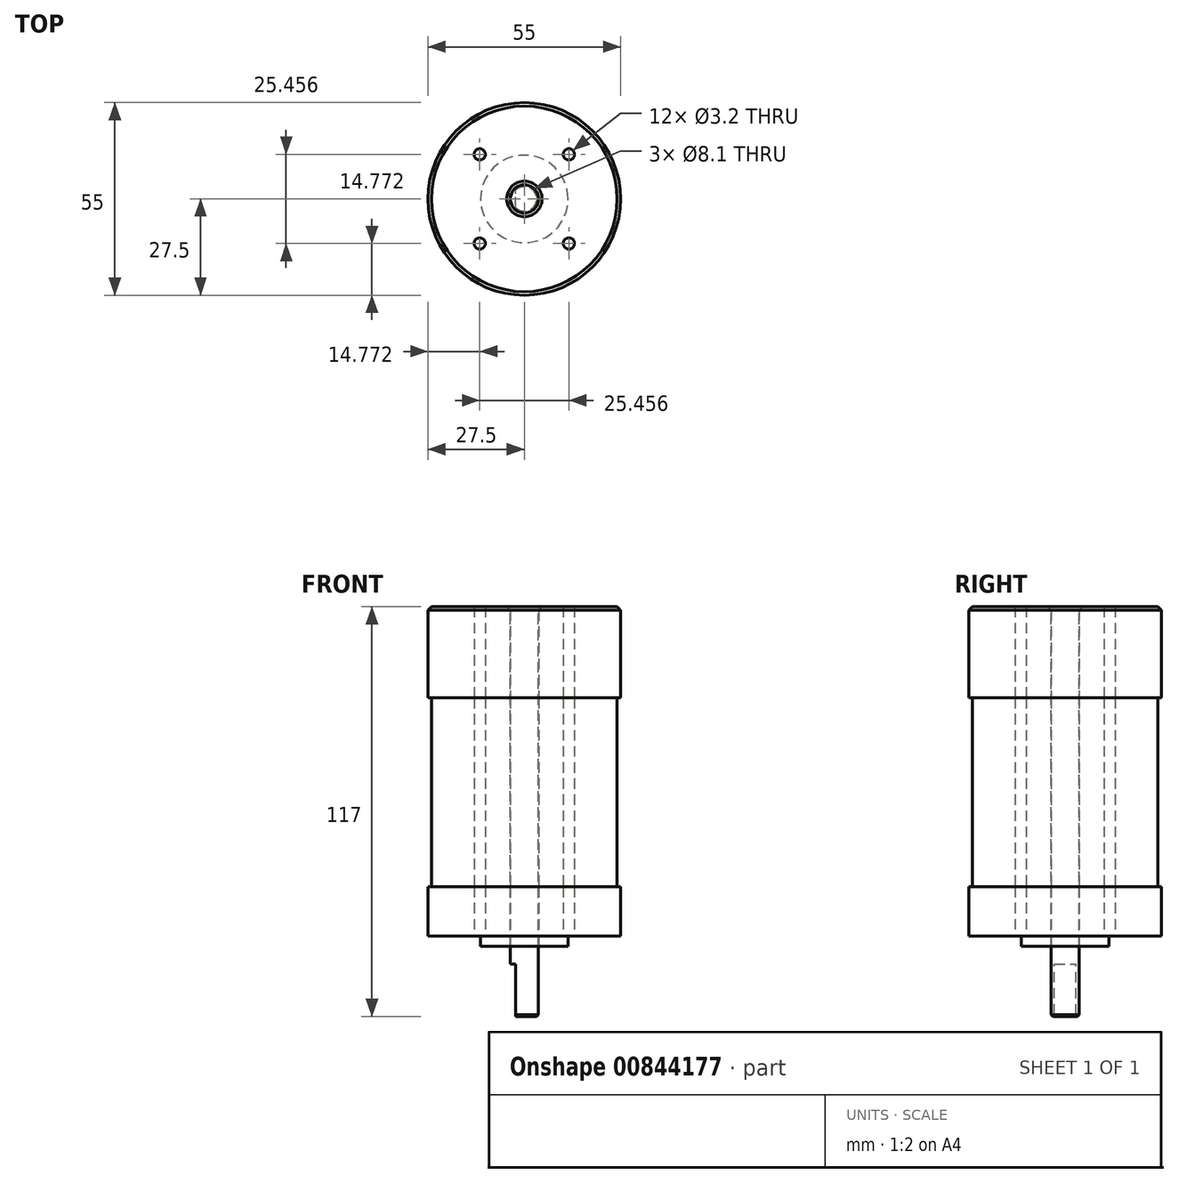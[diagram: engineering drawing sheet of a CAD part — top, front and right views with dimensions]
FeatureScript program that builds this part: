
annotation { "Feature Type Name" : "Feature", "Feature Type Description" : "" }
export const myFeature = defineFeature(function(context is Context, id is Id, definition is map)
    precondition{}
    {
        {
            var Q0;
            Q0=qCreatedBy(makeId("Top.planeOp"),FACE);
            var sketch = newSketch(context, id + "F0", { "sketchPlane" : qUnion([Q0])});
            skCircle(sketch, "E0", {"center": v(0, 0) * mm, "radius": 27.5 * mm});
            skSolve(sketch);
        }
        {
            var Q0;
            Q0=makeQuery(id+"F0.imprint","IMPRINT",FACE,{"disambiguationData":[TD([[makeQuery(id+"F0.imprint","IMPRINT",EDGE,{"derivedFrom":sQuery(id+"F0.wireOp",EDGE,"E0")}),1.0]])]});
            extrude(context, id + "F1", {"entities" : qUnion([Q0]), "depth" : 17 * mm, "offsetDistance" : 25 * mm});
        }
        {
            var Q0;
            Q0=makeQuery(id+"F1.opExtrude","CAP_FACE",FACE,{"disambiguationData":[OSD([sQuery(id+"F0.wireOp",EDGE,"E0")])],"isStart":true});
            var sketch = newSketch(context, id + "F2", { "sketchPlane" : qUnion([Q0])});
            skCircle(sketch, "E1", {"center": v(0, 0) * mm, "radius": 12.5 * mm});
            skSolve(sketch);
        }
        {
            var Q0;
            Q0=makeQuery(id+"F2.imprint","IMPRINT",FACE,{"disambiguationData":[TD([[makeQuery(id+"F2.imprint","IMPRINT",EDGE,{"derivedFrom":sQuery(id+"F2.wireOp",EDGE,"E1")}),-1.0]])]});
            extrude(context, id + "F3", {"entities" : qUnion([Q0]), "operationType" : NewBodyOperationType.REMOVE, "oppositeDirection" : true, "depth" : 3 * mm, "offsetDistance" : 25 * mm});
        }
        {
            var Q0;
            Q0=makeQuery(id+"F1.opExtrude","CAP_FACE",FACE,{"disambiguationData":[OSD([sQuery(id+"F0.wireOp",EDGE,"E0")])],"isStart":false});
            var sketch = newSketch(context, id + "F4", { "sketchPlane" : qUnion([Q0])});
            skCircle(sketch, "E2", {"center": v(0, 0) * mm, "radius": 26.5 * mm});
            skSolve(sketch);
        }
        {
            var Q0;
            Q0=makeQuery(id+"F4.imprint","IMPRINT",FACE,{"disambiguationData":[TD([[makeQuery(id+"F4.imprint","IMPRINT",EDGE,{"derivedFrom":sQuery(id+"F4.wireOp",EDGE,"E2")}),1.0]])]});
            extrude(context, id + "F5", {"entities" : qUnion([Q0]), "depth" : 54 * mm, "offsetDistance" : 25 * mm});
        }
        {
            var Q0;
            Q0=makeQuery(id+"F5.opExtrude","CAP_FACE",FACE,{"disambiguationData":[OSD([sQuery(id+"F4.wireOp",EDGE,"E2")])],"isStart":false});
            var sketch = newSketch(context, id + "F6", { "sketchPlane" : qUnion([Q0])});
            skCircle(sketch, "E3", {"center": v(0, 0) * mm, "radius": 27.5 * mm});
            skSolve(sketch);
        }
        {
            var Q0;
            Q0=qSketchRegion(id+"F6",true);
            extrude(context, id + "F7", {"entities" : qUnion([Q0]), "depth" : 26 * mm, "offsetDistance" : 25 * mm});
        }
        {
            var Q0;
            Q0=makeQuery(id+"F7.opExtrude","CAP_EDGE",EDGE,{"disambiguationData":[OSD([sQuery(id+"F6.wireOp",EDGE,"E3")])],"isStart":false});
            var Q1;
            Q1=makeQuery(id+"F3.boolean.opBoolean","COPY",EDGE,{"derivedFrom":makeQuery(id+"F3.opExtrude","CAP_EDGE",EDGE,{"disambiguationData":[OSD([sQuery(id+"F0.wireOp",EDGE,"E0")])],"isStart":false})});
            chamfer(context, id + "F8", {"entities" : qUnion([Q0, Q1]), "width" : 1 * mm, "tangentPropagation" : true});
        }
        {
            var Q0;
            Q0=makeQuery(id+"F1.opExtrude","CAP_FACE",FACE,{"disambiguationData":[OSD([sQuery(id+"F0.wireOp",EDGE,"E0")])],"isStart":true});
            var sketch = newSketch(context, id + "F9", { "sketchPlane" : qUnion([Q0])});
            skCircle(sketch, "E4", {"center": v(0, 0) * mm, "radius": 4.05 * mm});
            skSolve(sketch);
        }
        {
            var Q0;
            Q0=makeQuery(id+"F9.imprint","IMPRINT",FACE,{"disambiguationData":[TD([[makeQuery(id+"F9.imprint","IMPRINT",EDGE,{"derivedFrom":sQuery(id+"F9.wireOp",EDGE,"E4")}),1.0]])]});
            extrude(context, id + "F10", {"entities" : qUnion([Q0]), "operationType" : NewBodyOperationType.REMOVE, "endBound" : BoundingType.THROUGH_ALL, "oppositeDirection" : true, "depth" : 25 * mm, "offsetDistance" : 25 * mm});
        }
        {
            var Q0;
            Q0=makeQuery(id+"F10.boolean.opBoolean","INTERSECT",EDGE,{"derivedFrom":[makeQuery(id+"F7.opExtrude","CAP_FACE",FACE,{"disambiguationData":[OSD([sQuery(id+"F6.wireOp",EDGE,"E3")])],"isStart":false}),makeQuery(id+"F10.opExtrude","SWEPT_FACE",FACE,{"disambiguationData":[OSD([sQuery(id+"F9.wireOp",EDGE,"E4")])]})]});
            var Q1;
            Q1=makeQuery(id+"F10.boolean.opBoolean","COPY",EDGE,{"derivedFrom":makeQuery(id+"F10.opExtrude","CAP_EDGE",EDGE,{"disambiguationData":[OSD([sQuery(id+"F9.wireOp",EDGE,"E4")])],"isStart":true})});
            chamfer(context, id + "F11", {"entities" : qUnion([Q0, Q1]), "width" : 1 * mm, "tangentPropagation" : true});
        }
        {
            var Q0;
            Q0=makeQuery(id+"F7.opExtrude","CAP_FACE",FACE,{"disambiguationData":[OSD([sQuery(id+"F6.wireOp",EDGE,"E3")])],"isStart":false});
            var sketch = newSketch(context, id + "F12", { "sketchPlane" : qUnion([Q0])});
            skCircle(sketch, "E5", {"center": v(0, 0) * mm, "radius": 4 * mm});
            skSolve(sketch);
        }
        {
            var Q0;
            Q0=qSketchRegion(id+"F12",true);
            extrude(context, id + "F13", {"entities" : qUnion([Q0]), "oppositeDirection" : true, "depth" : 117 * mm, "offsetDistance" : 25 * mm});
        }
        {
            var Q0;
            Q0=makeQuery(id+"F13.opExtrude","CAP_EDGE",EDGE,{"disambiguationData":[OSD([sQuery(id+"F12.wireOp",EDGE,"E5")])],"isStart":false});
            chamfer(context, id + "F14", {"entities" : qUnion([Q0]), "width" : .5 * mm, "tangentPropagation" : true});
        }
        {
            var Q0;
            Q0=makeQuery(id+"F13.opExtrude","CAP_FACE",FACE,{"disambiguationData":[OSD([sQuery(id+"F12.wireOp",EDGE,"E5")])],"isStart":false});
            var sketch = newSketch(context, id + "F15", { "sketchPlane" : qUnion([Q0])});
            skArc(sketch, "E6", {"start": v(-2.5, 6.51) * mm, "mid": v(-6.98, 0) * mm, "end": v(-2.5, -6.51) * mm});
            skLineSegment(sketch, "E7", {"start": v(-2.5, 6.51) * mm, "end": v(-2.5, -6.51) * mm});
            skSolve(sketch);
        }
        {
            var Q0;
            Q0=qSketchRegion(id+"F15",true);
            extrude(context, id + "F16", {"entities" : qUnion([Q0]), "operationType" : NewBodyOperationType.REMOVE, "oppositeDirection" : true, "depth" : 15 * mm, "offsetDistance" : 25 * mm});
        }
        {
            var Q0;
            Q0=makeQuery(id+"F3.boolean.opBoolean","COPY",FACE,{"derivedFrom":makeQuery(id+"F3.opExtrude","CAP_FACE",FACE,{"disambiguationData":[OSD([sQuery(id+"F0.wireOp",EDGE,"E0"),sQuery(id+"F2.wireOp",EDGE,"E1")])],"isStart":false})});
            var sketch = newSketch(context, id + "F17", { "sketchPlane" : qUnion([Q0])});
            skCircle(sketch, "E8", {"center": v(0, 0) * mm, "radius": 18 * mm, "construction": true});
            skLineSegment(sketch, "E9", {"start": v(0, 0) * mm, "end": v(-26.42, 26.42) * mm, "construction": true});
            skCircle(sketch, "E10", {"center": v(-12.73, 12.73) * mm, "radius": 1.6 * mm});
            skCircle(sketch, "E11.1.0", {"center": v(-12.73, -12.73) * mm, "radius": 1.6 * mm});
            skCircle(sketch, "E11.2.0", {"center": v(12.73, -12.73) * mm, "radius": 1.6 * mm});
            skCircle(sketch, "E11.3.0", {"center": v(12.73, 12.73) * mm, "radius": 1.6 * mm});
            skSolve(sketch);
        }
        {
            var Q0;
            Q0=qSketchRegion(id+"F17",true);
            extrude(context, id + "F18", {"entities" : qUnion([Q0]), "operationType" : NewBodyOperationType.REMOVE, "endBound" : BoundingType.THROUGH_ALL, "oppositeDirection" : true, "depth" : 25 * mm, "offsetDistance" : 25 * mm});
        }
    });
